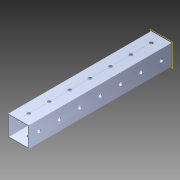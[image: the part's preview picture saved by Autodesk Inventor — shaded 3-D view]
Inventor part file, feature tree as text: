
AUTODESK INVENTOR PART (.ipt)
format: ipt  version: 2014 (Build 180170000, 170)  size: 1,149,952 bytes
history: native  units: in
note: dims shown in document units (in); Inventor stores cm internally (conversion verified against a paired STEP export)
features: pattern_circular x1, other x1, plane x1, extrude x1, imported_body x1, sketch x1
ambient origin geometry x8: Origin, YZ Plane, XZ Plane, XY Plane, X Axis, Y Axis, Z Axis, Center Point
bodies: Body1 (feature_tree)
feature tree (6):
  pattern_circular  "CirPattern2"
  other  "217-3426-STEP1"
  plane  "Work Plane1"
  extrude  "Extrusion1"  Depth=3937.0079in TaperAngle=0.0deg
  imported_body  "Base1"
  sketch  "Sketch1"  dims[d0=-7.0in d1=3937.0079in d2=0.0in]
